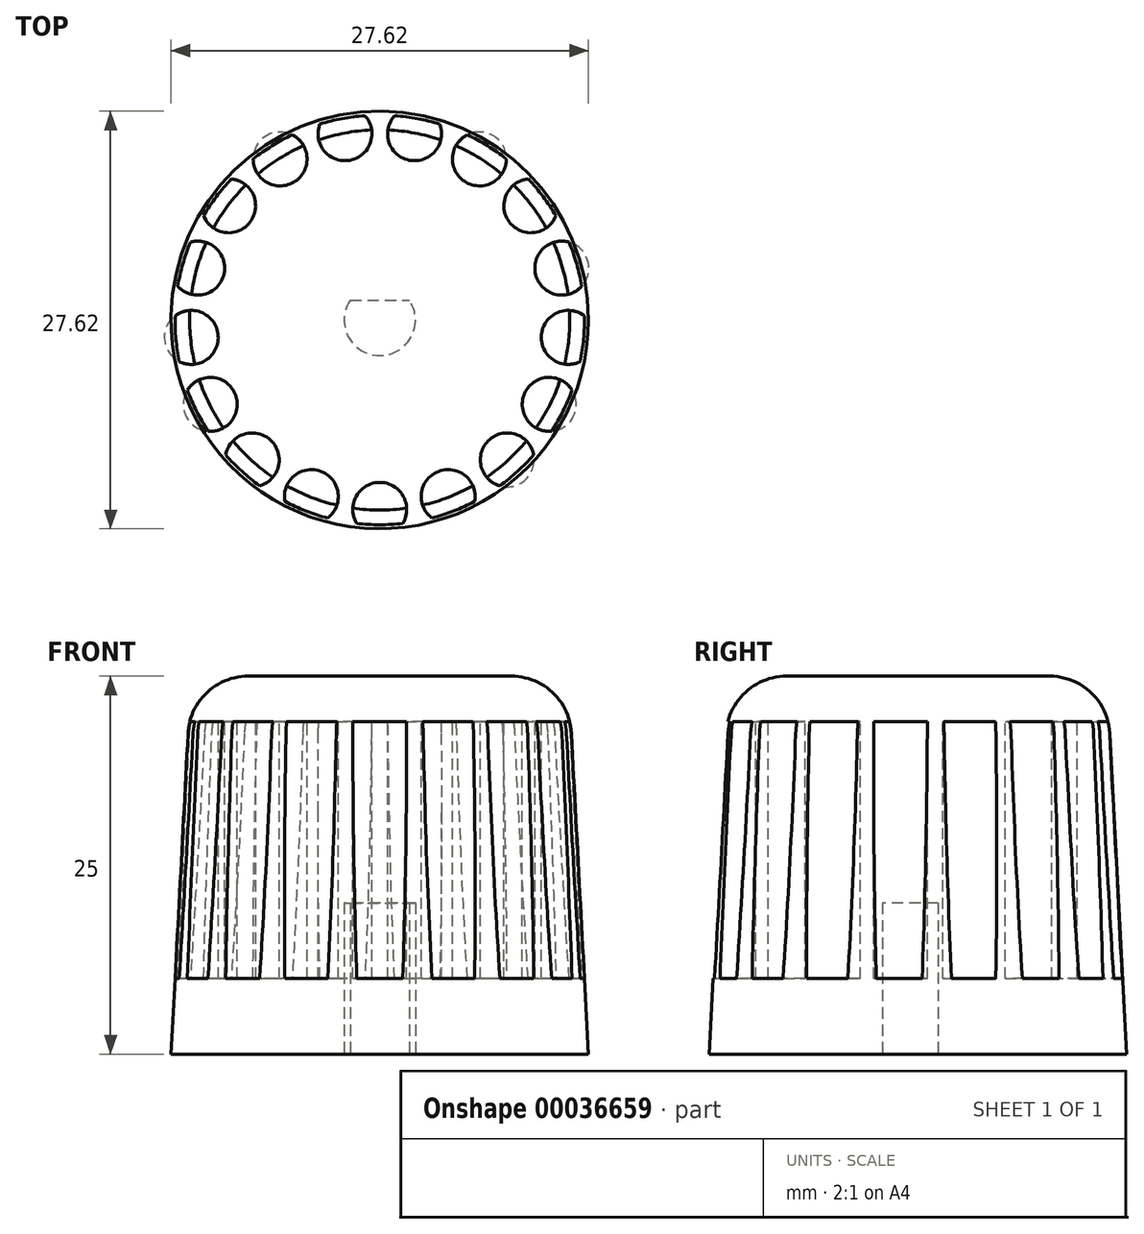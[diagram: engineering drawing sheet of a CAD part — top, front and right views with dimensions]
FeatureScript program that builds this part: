
annotation { "Feature Type Name" : "Feature", "Feature Type Description" : "" }
export const myFeature = defineFeature(function(context is Context, id is Id, definition is map)
    precondition{}
    {
        {
            var Q0;
            Q0=qCreatedBy(makeId("Top.planeOp"),FACE);
            cPlane(context, id + "F0", {"entities" : qUnion([Q0]), "cplaneType" : CPlaneType.OFFSET, "offset" : 3 * mm, "oppositeDirection" : true, "width" : 150 * mm, "height" : 150 * mm});
        }
        {
            var Q0;
            Q0=qCreatedBy(makeId("Top.planeOp"),FACE);
            var sketch = newSketch(context, id + "F1", { "sketchPlane" : qUnion([Q0])});
            skCircle(sketch, "E0", {"center": v(0, 0) * mm, "radius": 12.5 * mm});
            skSolve(sketch);
        }
        {
            var Q0;
            Q0 = qSketchRegion(id + "F1", true);
            extrude(context, id + "F2", {"entities" : qUnion([Q0]), "oppositeDirection" : true, "depth" : 25 * mm, "hasDraft" : true, "draftAngle" : 3 * degree});
        }
        {
            var Q0;
            Q0=qCreatedBy(id+"F0.planeOp",FACE);
            var sketch = newSketch(context, id + "F3", { "sketchPlane" : qUnion([Q0])});
            skCircle(sketch, "E1", {"center": v(0, -12.53) * mm, "radius": 1.78 * mm});
            skCircle(sketch, "E2.1.0", {"center": v(4.53, -11.68) * mm, "radius": 1.78 * mm});
            skCircle(sketch, "E2.2.0", {"center": v(8.44, -9.26) * mm, "radius": 1.78 * mm});
            skCircle(sketch, "E2.3.0", {"center": v(11.21, -5.58) * mm, "radius": 1.78 * mm});
            skCircle(sketch, "E2.4.0", {"center": v(12.47, -1.16) * mm, "radius": 1.78 * mm});
            skCircle(sketch, "E2.5.0", {"center": v(12.05, 3.43) * mm, "radius": 1.78 * mm});
            skCircle(sketch, "E2.6.0", {"center": v(10, 7.55) * mm, "radius": 1.78 * mm});
            skCircle(sketch, "E2.7.0", {"center": v(6.6, 10.65) * mm, "radius": 1.78 * mm});
            skCircle(sketch, "E2.8.0", {"center": v(2.3, 12.31) * mm, "radius": 1.78 * mm});
            skCircle(sketch, "E2.9.0", {"center": v(-2.3, 12.31) * mm, "radius": 1.78 * mm});
            skPoint(sketch, "E2.center", {"position": v(0, 0) * mm});
            skCircle(sketch, "E3.1.10.0", {"center": v(-6.6, 10.65) * mm, "radius": 1.78 * mm});
            skCircle(sketch, "E3.1.11.0", {"center": v(-10, 7.55) * mm, "radius": 1.78 * mm});
            skCircle(sketch, "E3.1.12.0", {"center": v(-12.05, 3.43) * mm, "radius": 1.78 * mm});
            skCircle(sketch, "E3.1.13.0", {"center": v(-12.47, -1.16) * mm, "radius": 1.78 * mm});
            skCircle(sketch, "E3.1.14.0", {"center": v(-11.21, -5.58) * mm, "radius": 1.78 * mm});
            skCircle(sketch, "E3.1.15.0", {"center": v(-8.44, -9.26) * mm, "radius": 1.78 * mm});
            skCircle(sketch, "E3.1.16.0", {"center": v(-4.53, -11.68) * mm, "radius": 1.78 * mm});
            skSolve(sketch);
        }
        {
            var Q0;
            Q0 = qSketchRegion(id + "F3", true);
            extrude(context, id + "F4", {"entities" : qUnion([Q0]), "operationType" : NewBodyOperationType.REMOVE, "oppositeDirection" : true, "depth" : 17 * mm});
        }
        {
            var Q0;
            Q0=makeQuery(id+"F2.opExtrude","CAP_FACE",FACE,{"disambiguationData":[OSD([sQuery(id+"F1.wireOp",EDGE,"E0")])],"isStart":true});
            fillet(context, id + "F5", {"entities" : qUnion([Q0]), "radius" : 4 * mm, "tangentPropagation" : true, "allowEdgeOverflow" : false});
        }
        {
            var Q0;
            Q0=makeQuery(id+"F2.opExtrude","CAP_FACE",FACE,{"disambiguationData":[OSD([sQuery(id+"F1.wireOp",EDGE,"E0")])],"isStart":false});
            var sketch = newSketch(context, id + "F6", { "sketchPlane" : qUnion([Q0])});
            skArc(sketch, "E4", {"start": v(1.96, -1.32) * mm, "mid": v(0, 2.36) * mm, "end": v(-1.96, -1.32) * mm});
            skLineSegment(sketch, "E5", {"start": v(-1.96, -1.32) * mm, "end": v(1.96, -1.32) * mm});
            skSolve(sketch);
        }
        {
            var Q0;
            Q0=makeQuery(id+"F6.imprint","IMPRINT",FACE,{"disambiguationData":[TD([[makeQuery(id+"F6.imprint","IMPRINT",EDGE,{"derivedFrom":sQuery(id+"F6.wireOp",EDGE,"E4")}),1.0]])]});
            extrude(context, id + "F7", {"entities" : qUnion([Q0]), "operationType" : NewBodyOperationType.REMOVE, "oppositeDirection" : true, "depth" : 10 * mm});
        }
    });
